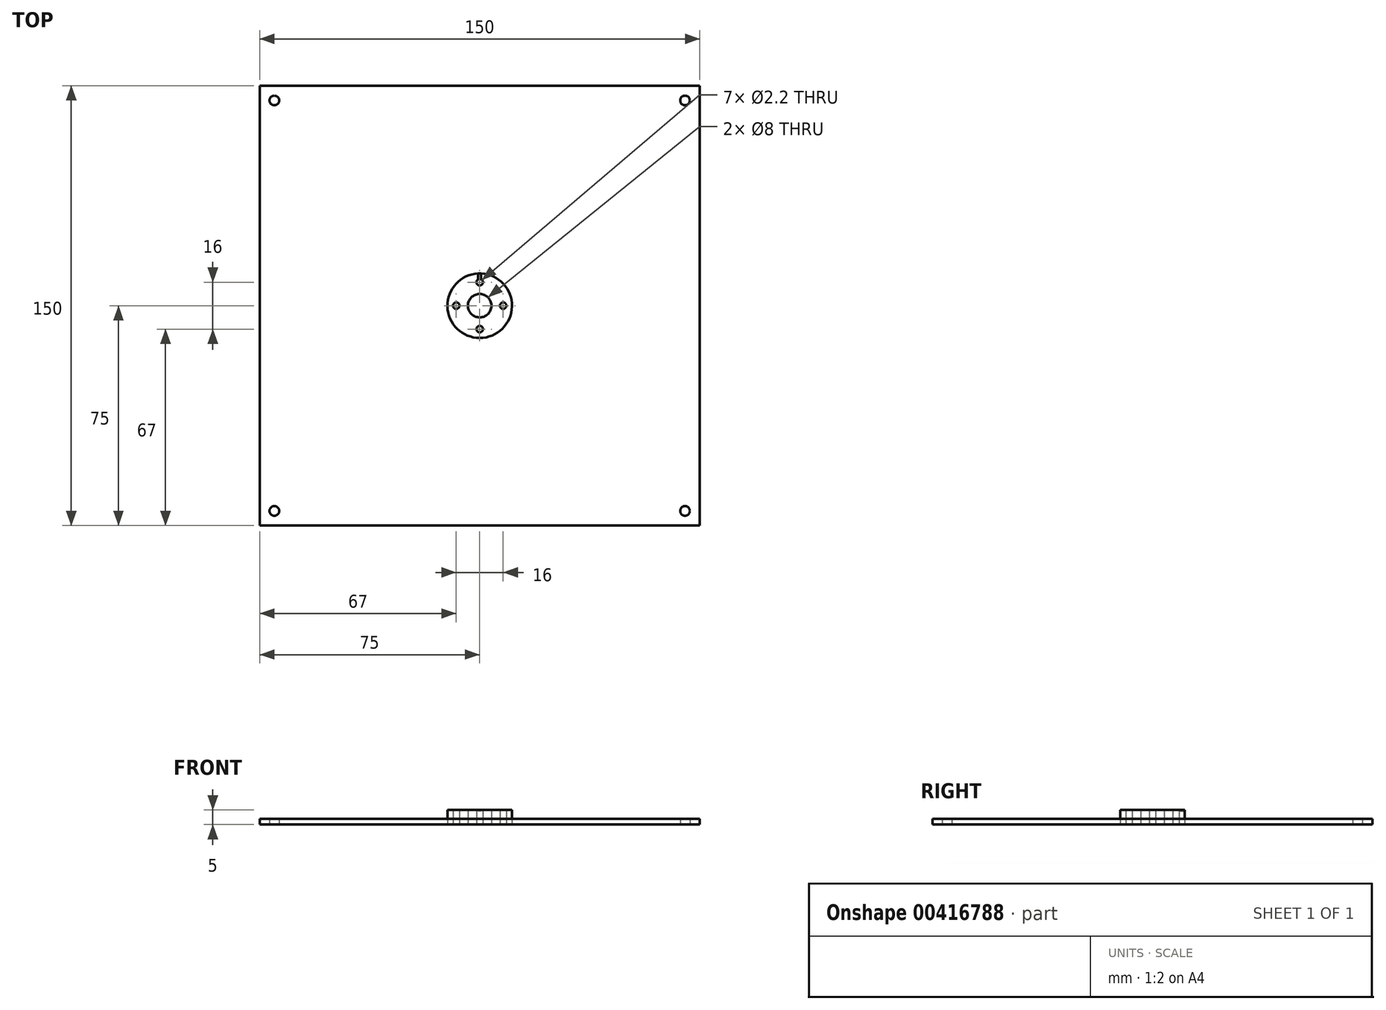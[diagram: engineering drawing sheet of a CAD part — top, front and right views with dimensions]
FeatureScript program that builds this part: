
annotation { "Feature Type Name" : "Feature", "Feature Type Description" : "" }
export const myFeature = defineFeature(function(context is Context, id is Id, definition is map)
    precondition{}
    {
        {
            var Q0;
            Q0=qCreatedBy(makeId("Top.planeOp"),FACE);
            var sketch = newSketch(context, id + "F0", { "sketchPlane" : qUnion([Q0])});
            skCircle(sketch, "E0.cCircle", {"center": v(0, 0) * mm, "radius": 75 * mm, "construction": true});
            skLineSegment(sketch, "E0.0", {"start": v(-75, 75) * mm, "end": v(75, 75) * mm});
            skLineSegment(sketch, "E0.1", {"start": v(75, 75) * mm, "end": v(75, -75) * mm});
            skLineSegment(sketch, "E0.2", {"start": v(75, -75) * mm, "end": v(-75, -75) * mm});
            skLineSegment(sketch, "E0.3", {"start": v(-75, -75) * mm, "end": v(-75, 75) * mm});
            skPoint(sketch, "E0.0.midPoint", {"position": v(0, 75) * mm});
            skCircle(sketch, "E1", {"center": v(0, 0) * mm, "radius": 8 * mm, "construction": true});
            skPoint(sketch, "E2", {"position": v(0, 8) * mm});
            skPoint(sketch, "E3", {"position": v(0, -8) * mm});
            skPoint(sketch, "E4", {"position": v(8, 0) * mm});
            skPoint(sketch, "E5", {"position": v(-8, 0) * mm});
            skCircle(sketch, "E6", {"center": v(0, 0) * mm, "radius": 4 * mm});
            skPoint(sketch, "E7", {"position": v(-70, 70) * mm});
            skPoint(sketch, "E8", {"position": v(70, 70) * mm});
            skPoint(sketch, "E9", {"position": v(70, -70) * mm});
            skPoint(sketch, "E10", {"position": v(-70, -70) * mm});
            skSolve(sketch);
        }
        {
            var Q0;
            Q0 = qSketchRegion(id + "F0", true);
            extrude(context, id + "F1", {"entities" : qUnion([Q0]), "depth" : 2 * mm});
        }
        {
            var Q0;
            Q0=sQuery(id+"F0.wireOp",VERTEX,"E2");
            var Q1;
            Q1=sQuery(id+"F0.wireOp",VERTEX,"E5");
            var Q2;
            Q2=sQuery(id+"F0.wireOp",VERTEX,"E3");
            var Q3;
            Q3=sQuery(id+"F0.wireOp",VERTEX,"E4");
            var Q4;
            Q4=makeQuery(id+"F1.opExtrude","SWEPT_BODY",BODY,{"disambiguationData":[OSD([sQuery(id+"F0.wireOp",EDGE,"E0.0"),sQuery(id+"F0.wireOp",EDGE,"E0.1"),sQuery(id+"F0.wireOp",EDGE,"E0.2"),sQuery(id+"F0.wireOp",EDGE,"E0.3")])]});
            hole(context, id + "F2", {"style" : HoleStyle.SIMPLE, "endStyle" : HoleEndStyle.THROUGH, "oppositeDirection" : true, "holeDiameter" : 2.2 * mm, "isTappedThrough" : true, "tappedDepth" : 6.2 * mm, "tapClearance" : 3, "locations" : qUnion([Q0, Q1, Q2, Q3]), "scope" : qUnion([Q4])});
        }
        {
            var Q0;
            Q0=sQuery(id+"F0.wireOp",VERTEX,"E7");
            var Q1;
            Q1=sQuery(id+"F0.wireOp",VERTEX,"E10");
            var Q2;
            Q2=sQuery(id+"F0.wireOp",VERTEX,"E9");
            var Q3;
            Q3=sQuery(id+"F0.wireOp",VERTEX,"E8");
            var Q4;
            Q4=makeQuery(id+"F1.opExtrude","SWEPT_BODY",BODY,{"disambiguationData":[OSD([sQuery(id+"F0.wireOp",EDGE,"E0.0"),sQuery(id+"F0.wireOp",EDGE,"E0.1"),sQuery(id+"F0.wireOp",EDGE,"E0.2"),sQuery(id+"F0.wireOp",EDGE,"E0.3"),sQuery(id+"F0.wireOp",EDGE,"E6")])]});
            hole(context, id + "F3", {"style" : HoleStyle.SIMPLE, "endStyle" : HoleEndStyle.THROUGH, "oppositeDirection" : true, "standardTappedOrClearance" : lookupTablePath({ "standard" : "ISO", "fit" : "Normal", "size" : "M3", "type" : "Clearance" }), "standardBlindInLast" : lookupTablePath({ "fit" : "Standard", "standard" : "ISO", "size" : "M3", "type" : "Clearance" }), "holeDiameter" : 3.3 * mm, "isTappedThrough" : true, "tappedDepth" : 6.2 * mm, "tapClearance" : 3, "locations" : qUnion([Q0, Q1, Q2, Q3]), "scope" : qUnion([Q4])});
        }
        {
            var Q0;
            Q0=qCreatedBy(makeId("Top.planeOp"),FACE);
            var sketch = newSketch(context, id + "F4", { "sketchPlane" : qUnion([Q0])});
            skCircle(sketch, "E11", {"center": v(0, 0) * mm, "radius": 11 * mm});
            skCircle(sketch, "E12", {"center": v(0, 0) * mm, "radius": 8 * mm, "construction": true});
            skPoint(sketch, "E13", {"position": v(0, 8) * mm});
            skPoint(sketch, "E14", {"position": v(-8, 0) * mm});
            skPoint(sketch, "E15", {"position": v(0, -8) * mm});
            skPoint(sketch, "E16", {"position": v(8, 0) * mm});
            skCircle(sketch, "E17", {"center": v(0, 0) * mm, "radius": 4 * mm});
            skSolve(sketch);
        }
        {
            var Q0;
            Q0 = qSketchRegion(id + "F4", true);
            extrude(context, id + "F5", {"entities" : qUnion([Q0]), "depth" : 5 * mm});
        }
        {
            var Q0;
            Q0=sQuery(id+"F4.wireOp",VERTEX,"E15");
            var Q1;
            Q1=sQuery(id+"F4.wireOp",VERTEX,"E16");
            var Q2;
            Q2=sQuery(id+"F4.wireOp",VERTEX,"E13");
            var Q3;
            Q3=sQuery(id+"F4.wireOp",VERTEX,"E14");
            var Q4;
            Q4=makeQuery(id+"F5.opExtrude","SWEPT_BODY",BODY,{"disambiguationData":[OSD([sQuery(id+"F4.wireOp",EDGE,"E11")])]});
            hole(context, id + "F6", {"style" : HoleStyle.SIMPLE, "endStyle" : HoleEndStyle.THROUGH, "oppositeDirection" : true, "holeDiameter" : 2.2 * mm, "isTappedThrough" : true, "tappedDepth" : 6.2 * mm, "tapClearance" : 3, "locations" : qUnion([Q0, Q1, Q2, Q3]), "scope" : qUnion([Q4])});
        }
        {
            var Q0;
            Q0=makeQuery(id+"F5.opExtrude","CAP_FACE",FACE,{"disambiguationData":[OSD([sQuery(id+"F4.wireOp",EDGE,"E11"),sQuery(id+"F4.wireOp",EDGE,"E17")])],"isStart":false});
            var sketch = newSketch(context, id + "F7", { "sketchPlane" : qUnion([Q0])});
            skLineSegment(sketch, "E18", {"start": v(0, 0) * mm, "end": v(0, 11) * mm, "construction": true});
            skLineSegment(sketch, "E19", {"start": v(-0.5, 8.98) * mm, "end": v(-0.5, 11) * mm});
            skLineSegment(sketch, "E20", {"start": v(0.5, 10.99) * mm, "end": v(0.5, 8.98) * mm});
            skSolve(sketch);
        }
        {
            var Q0;
            {var subQ6=sQuery(id+"F7.wireOp",EDGE,"E20");Q0=makeQuery(id+"F7.imprint","IMPRINT",FACE,{"disambiguationData":[TD([[makeQuery(id+"F7.imprint","IMPRINT",EDGE,{"derivedFrom":subQ6}),-1.0]])]});}
            extrude(context, id + "F8", {"entities" : qUnion([Q0]), "operationType" : NewBodyOperationType.REMOVE, "oppositeDirection" : true, "depth" : 0.4 * mm});
        }
    });
